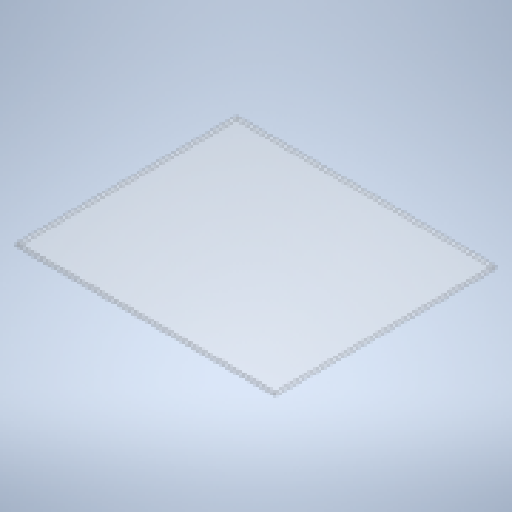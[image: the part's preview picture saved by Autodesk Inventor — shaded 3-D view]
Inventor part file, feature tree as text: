
AUTODESK INVENTOR PART (.ipt)
format: ipt  version: 2023.1 (Build 271208000, 208)  size: 237,056 bytes
history: native  units: mm
features: other x1, extrude x1, sketch x1
ambient origin geometry x8: Origin, YZ Plane, XZ Plane, XY Plane, X Axis, Y Axis, Z Axis, Center Point
bodies: Body1 (feature_tree)
feature tree (3):
  other  "ソリッド1"
  extrude  "押し出し1"  Depth=200.0mm
  sketch  "スケッチ1"
